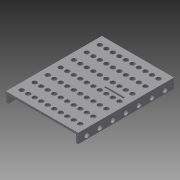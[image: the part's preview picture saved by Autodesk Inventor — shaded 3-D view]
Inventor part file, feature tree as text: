
AUTODESK INVENTOR PART (.ipt)
format: ipt  version: 2015 (Build 190159000, 159)  size: 338,944 bytes
history: native  units: in
note: dims shown in document units (in); Inventor stores cm internally (conversion verified against a paired STEP export)
features: extrude x13, sketch x13, pattern_linear x5
ambient origin geometry x8: Origin, YZ Plane, XZ Plane, XY Plane, X Axis, Y Axis, Z Axis, Center Point
bodies: Solid1 (feature_tree)
feature tree (31):
  extrude  "Extrusion1"  Depth=3.4744in
  extrude  "Extrusion2"  Depth=0.0787in
  pattern_linear  "Rectangular Pattern1"  Count1=15 Spacing1=0.2362in
  extrude  "Extrusion3"  Depth=0.122in TaperAngle=0.0deg
  extrude  "Extrusion4"  Depth=0.0787in
  extrude  "Extrusion5"  Depth=0.0787in
  extrude  "Extrusion6"  Depth=0.2756in
  extrude  "Extrusion7"  Depth=0.0837in
  pattern_linear  "Rectangular Pattern2"  Count1=15 Spacing1=0.2362in
  extrude  "Extrusion11"  Depth=0.0787in TaperAngle=0.0deg
  pattern_linear  "Rectangular Pattern3"  Count1=9 Spacing1=0.4724in
  extrude  "Extrusion12"  Depth=0.0787in TaperAngle=0.0deg
  extrude  "Extrusion13"  Depth=0.0787in
  pattern_linear  "Rectangular Pattern4"  Spacing1=0.0787in  [1 undecoded]
  extrude  "Extrusion14"  Depth=0.0787in
  pattern_linear  "Rectangular Pattern5"  Spacing1=0.1673in  [1 undecoded]
  extrude  "Extrusion15"  Depth=0.0787in TaperAngle=0.0deg
  extrude  "Extrusion16"  Depth=0.0787in
  sketch  "Sketch1"  dims[d0=2.4508in d1=3.4744in]
  sketch  "Sketch2"  dims[d2=0.0787in d3=0.0in d4=0.0074in]
  sketch  "Sketch3"  dims[d7=0.1673in]
  sketch  "Sketch4"  dims[d8=0.0787in d9=0.0in d10=5.9055in d12=0.2362in]
  sketch  "Sketch5"  dims[d13=3.937in d15=0.2362in d16=0.122in d17=0.0in]
  sketch  "Sketch6"  dims[d18=0.0433in d19=0.0in d20=0.0787in]
  sketch  "Sketch7"  dims[d21=0.2756in d22=0.0in d23=0.0787in]
  sketch  "Sketch11"  dims[d24=0.2756in d25=0.0in d26=0.0344in]
  sketch  "Sketch12"  dims[d27=0.0837in d28=0.0837in]
  sketch  "Sketch13"  dims[d29=0.1673in]
  sketch  "Sketch14"  dims[d30=0.2756in d31=0.0in d32=5.9055in d34=0.2362in]
  sketch  "Sketch15"  dims[d42=0.1673in d43=0.0787in d44=0.0in d45=3.5433in d47=0.4724in]
  sketch  "Sketch16"  dims[d48=3.937in d50=0.2362in d51=0.0787in d52=0.0in d54=0.1673in d55=0.0787in d56=0.0in d57=3.5433in d59=0.4724in d61=0.1673in d62=0.0787in d63=0.0in d64=3.5433in d66=0.4724in d67=0.0787in d68=0.0in d70=0.7087in d71=0.0591in d72=0.0787in d73=0.0in]
note: 2 required parameter values undecoded (feature->parameter linkage not recoverable at this tier; creation-order binding heuristic only, values carry confidence <= 0.55)
